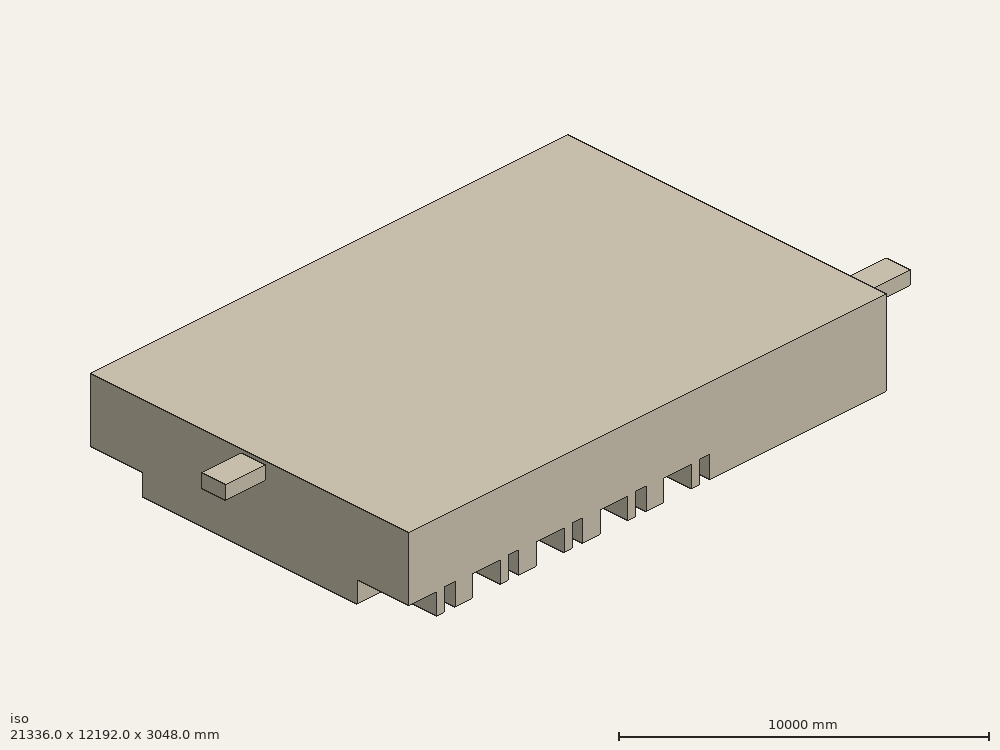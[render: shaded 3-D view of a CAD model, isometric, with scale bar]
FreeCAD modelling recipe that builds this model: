
FCSTD DOCUMENT  (FreeCAD 0.18R14555 (Git shallow))
Label: simple_case_domain
License: All rights reserved
LicenseURL: http://en.wikipedia.org/wiki/All_rights_reserved
objects: Part::Box×14, Part::MultiFuse×8, Part::FeaturePython×2, Part::Mirroring×1
note: 25 computed .brp shape members not serialized (recipe doc carries the construction recipe); baked Part::Feature solids carry a one-line shape summary decoded from their .brp

FEATURE [Part::Box] Box  label="Room"
  AttacherType = Attacher::AttachEngine3D
  Height = 3048
  Length = 18288
  Width = 12192
FEATURE [Part::Box] Box001  label="Bed 1"
  AttacherType = Attacher::AttachEngine3D
  Height = 762
  Length = 1066.8
  Width = 1981.2
FEATURE [Part::Box] Box002  label="Table 1"
  AttacherType = Attacher::AttachEngine3D
  Height = 798.576
  Length = 396.24
  Placement = pos=(1371.6,0,0) rot=(0,0,1;0rad)
  Width = 396.24
FEATURE [Part::MultiFuse] Fusion  label="Set 1"
  Shapes = -> [Box002,Box001]
FEATURE [Part::Box] Box003  label="Bed 002"
  AttacherType = Attacher::AttachEngine3D
  Height = 762
  Length = 1066.8
  Width = 1981.2
FEATURE [Part::Box] Box004  label="Table 002"
  AttacherType = Attacher::AttachEngine3D
  Height = 798.576
  Length = 396.24
  Placement = pos=(1371.6,0,0) rot=(0,0,1;0rad)
  Width = 396.24
FEATURE [Part::MultiFuse] Fusion001  label="Set 2"
  Placement = pos=(2438.4,0,0) rot=(0,0,1;0rad)
  Shapes = -> [Box004,Box003]
FEATURE [Part::Box] Box005  label="Table 003"
  AttacherType = Attacher::AttachEngine3D
  Height = 798.576
  Length = 396.24
  Placement = pos=(1371.6,0,0) rot=(0,0,1;0rad)
  Width = 396.24
FEATURE [Part::Box] Box006  label="Bed 003"
  AttacherType = Attacher::AttachEngine3D
  Height = 762
  Length = 1066.8
  Width = 1981.2
FEATURE [Part::MultiFuse] Fusion002  label="Set 3"
  Placement = pos=(4876.8,0,0) rot=(0,0,1;0rad)
  Shapes = -> [Box005,Box006]
FEATURE [Part::Box] Box007  label="Bed 004"
  AttacherType = Attacher::AttachEngine3D
  Height = 762
  Length = 1066.8
  Width = 1981.2
FEATURE [Part::Box] Box008  label="Table 004"
  AttacherType = Attacher::AttachEngine3D
  Height = 798.576
  Length = 396.24
  Placement = pos=(1371.6,0,0) rot=(0,0,1;0rad)
  Width = 396.24
FEATURE [Part::MultiFuse] Fusion003  label="Set 4"
  Placement = pos=(7315.2,0,0) rot=(0,0,1;0rad)
  Shapes = -> [Box008,Box007]
FEATURE [Part::Box] Box009  label="Table 005"
  AttacherType = Attacher::AttachEngine3D
  Height = 798.576
  Length = 396.24
  Placement = pos=(1371.6,0,0) rot=(0,0,1;0rad)
  Width = 396.24
FEATURE [Part::Box] Box010  label="Bed 005"
  AttacherType = Attacher::AttachEngine3D
  Height = 762
  Length = 1066.8
  Width = 1981.2
FEATURE [Part::MultiFuse] Fusion004  label="Set 5"
  Placement = pos=(9753.6,0,0) rot=(0,0,1;0rad)
  Shapes = -> [Box009,Box010]
FEATURE [Part::MultiFuse] Fusion005  label="right beds"
  Shapes = -> [Fusion001,Fusion002,Fusion003,Fusion004,Fusion]
FEATURE [Part::Mirroring] Part__Mirroring  label="left beds"
  Base = (0,6096,0)
  Normal = (0,1,0)
  Source = -> Fusion005
FEATURE [Part::Box] Box011  label="Nurse Station"
  AttacherType = Attacher::AttachEngine3D
  Height = 1219.2
  Length = 3048
  Placement = pos=(15240,7620,0) rot=(0,0,1;0rad)
  Width = 4572
FEATURE [Part::Box] Box012  label="main inlet"
  AttacherType = Attacher::AttachEngine3D
  Height = 487.68
  Length = 2438.4
  Placement = pos=(17373.6,609.6,2438.4) rot=(0,0,1;0rad)
  Width = 914.4
FEATURE [Part::Box] Box013  label="main outlet"
  AttacherType = Attacher::AttachEngine3D
  Height = 487.68
  Length = 2438.4
  Placement = pos=(-1524,5486.4,2438.4) rot=(0,0,1;0rad)
  Width = 914.4
FEATURE [Part::MultiFuse] Fusion006  label="all beds"
  Shapes = -> [Part__Mirroring,Fusion005]
FEATURE [Part::FeaturePython] XOR  label="volume"  # WARN: FeaturePython — macro-defined, semantics opaque (R4)
  Objects = -> [Fusion006,Box,Box011]
  Tolerance = 0
FEATURE [Part::MultiFuse] Fusion008  label="all vents"
  Shapes = -> [Box013,Box012]
FEATURE [Part::FeaturePython] XOR001  label="flow_domain"  # WARN: FeaturePython — macro-defined, semantics opaque (R4)
  Objects = -> [Fusion008,XOR]
  Tolerance = 0
